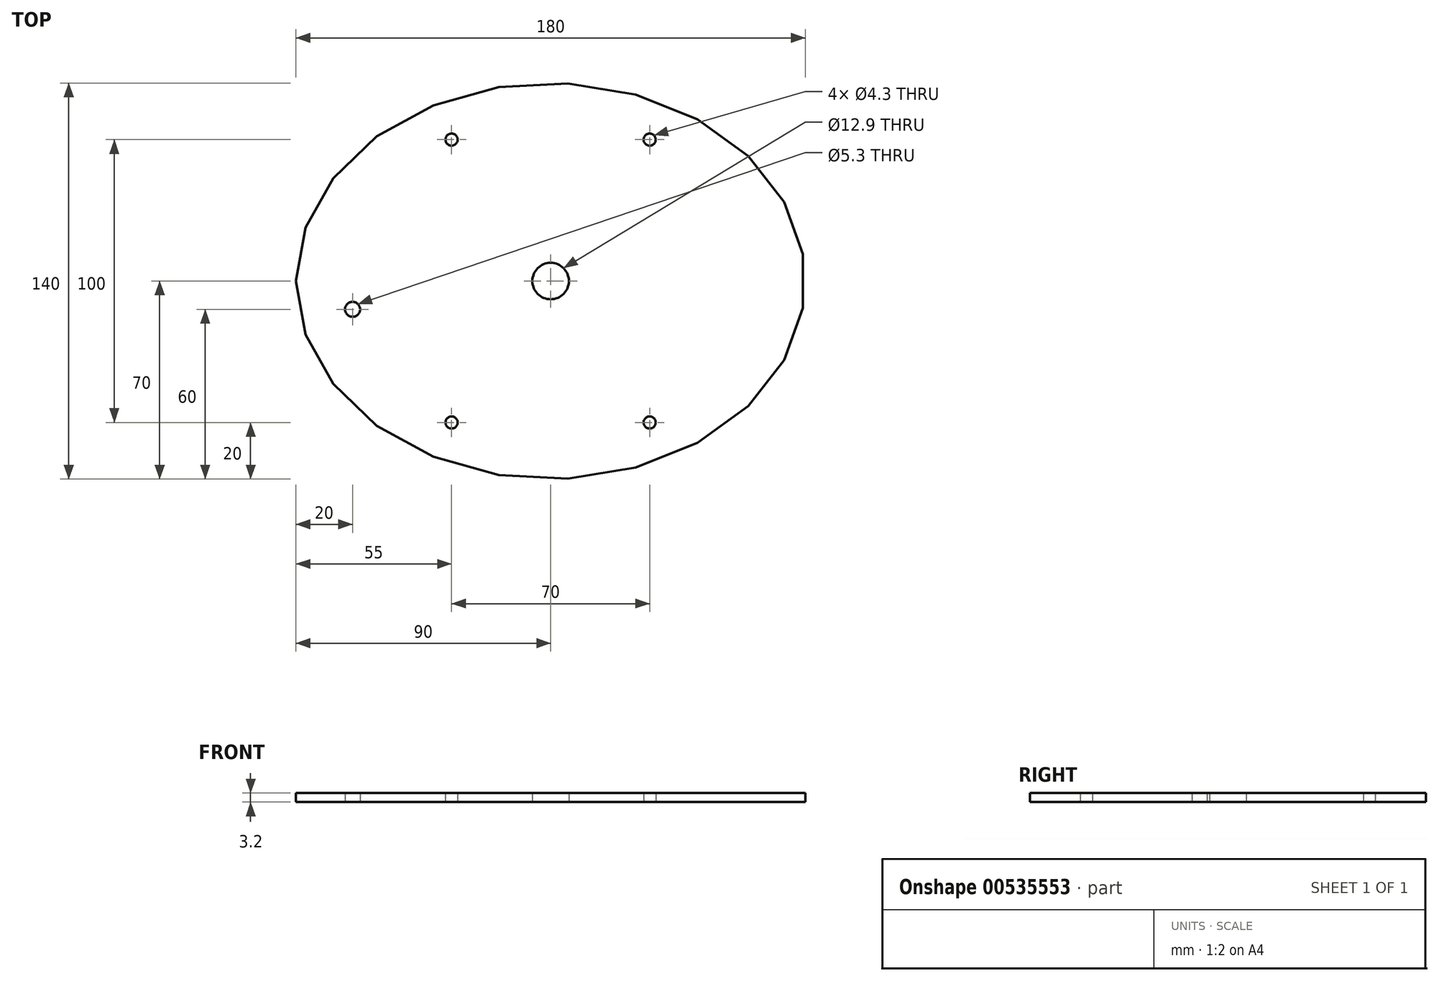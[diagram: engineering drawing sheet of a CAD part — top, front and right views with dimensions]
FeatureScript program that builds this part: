
annotation { "Feature Type Name" : "Feature", "Feature Type Description" : "" }
export const myFeature = defineFeature(function(context is Context, id is Id, definition is map)
    precondition{}
    {
        {
            var Q0;
            Q0=qCreatedBy(makeId("Top.planeOp"),FACE);
            var sketch = newSketch(context, id + "F0", { "sketchPlane" : qUnion([Q0])});
            skEllipse(sketch, "E0", {"center": v(0, 0) * mm, "majorRadius": 90 * mm, "minorRadius": 70 * mm, "majorAxis": v(-1, 0)});
            skCircle(sketch, "E1", {"center": v(0, 0) * mm, "radius": 6.45 * mm});
            skCircle(sketch, "E2", {"center": v(-70, -10) * mm, "radius": 2.65 * mm});
            skCircle(sketch, "E3", {"center": v(-35, 50) * mm, "radius": 2.15 * mm});
            skCircle(sketch, "E4.MirrorC", {"center": v(-35, -50) * mm, "radius": 2.15 * mm});
            skCircle(sketch, "E5.MirrorC", {"center": v(35, 50) * mm, "radius": 2.15 * mm});
            skCircle(sketch, "E6.MirrorC", {"center": v(35, -50) * mm, "radius": 2.15 * mm});
            skSolve(sketch);
        }
        {
            var Q0;
            Q0 = qSketchRegion(id + "F0", true);
            extrude(context, id + "F1", {"entities" : qUnion([Q0]), "depth" : 3.2 * mm, "offsetDistance" : 25 * mm});
        }
    });
